# Revit family: LUXT-(NH)(NDL)(NDR)(OPT)
name_source: partatom
category: Generic Models
revit_build: Autodesk Revit Architecture 2012 (Build: 20110309_2315(x64)
units: mm (PartAtom-declared; Revit-internal decimal feet)

## types (1)
- LUXT-(NH)(NDL)(NDR)(OPT)
    A-1 Shelf On/Off = No
    A-10 Shelf On/Off = No
    A-11 Shelf On/Off = No
    A-2 Shelf On/Off = Yes
    A-3 Shelf On/Off = No
    A-4 Shelf On/Off = Yes
    A-5 Shelf On/Off = No
    A-6 Shelf On/Off = Yes
    A-7 Shelf On/Off = No
    A-8 Shelf On/Off = No
    A-9 Shelf On/Off = No
    B-1 Shelf On/Off = No
    B-10 Shelf On/Off = No
    B-11 Shelf On/Off = No
    B-2 Shelf On/Off = Yes
    B-3 Shelf On/Off = No
    B-4 Shelf On/Off = Yes
    B-5 Shelf On/Off = No
    B-6 Shelf On/Off = Yes
    B-7 Shelf On/Off = No
    B-8 Shelf On/Off = No
    B-9 Shelf On/Off = No
    Back Panel Material = Default Madix
    Frame Height = 5' - 0"
    Frame Material = Default Madix
    Frame Width = 4' - 0"
    Material of Legs = Default Madix
    Model = Luxe T-Uprights with Legs on Both Sides
    Nominal Depth of Leg = 3' - 6"
    Shelf Depth = 1' - 6"
    Shelf Material = Default Madix
    URL = http://www.madixinc.com

## geometry (parser evidence)
native form markers: Blend x4, Sweep x35
no freeform markers — native parametric forms only
